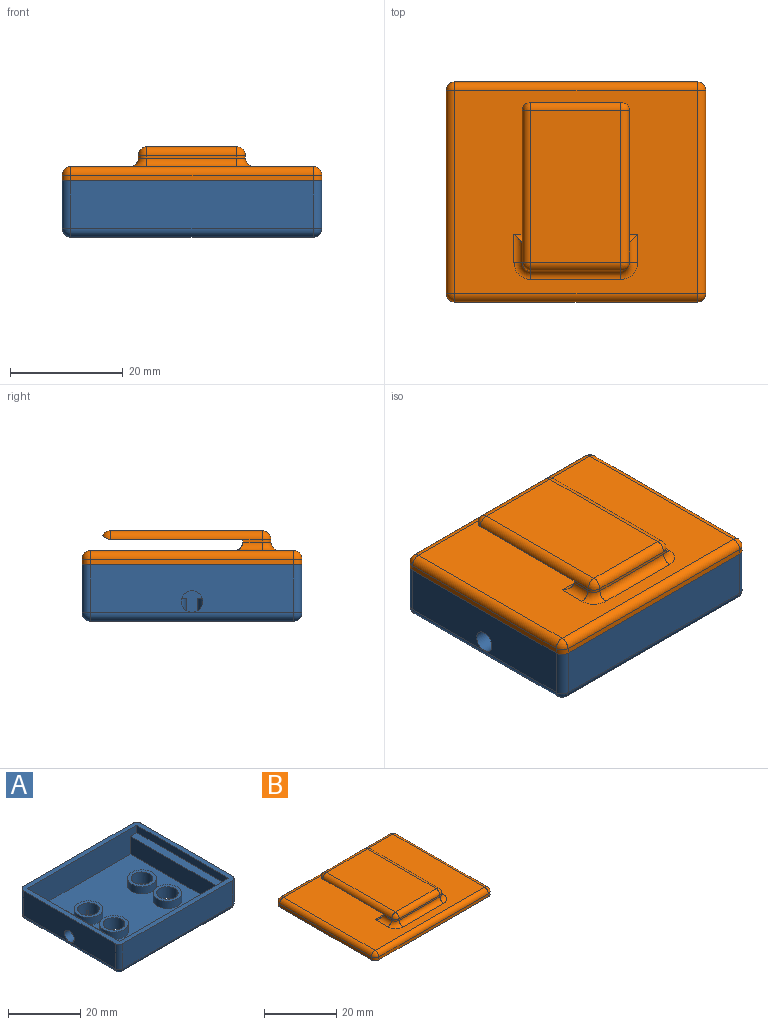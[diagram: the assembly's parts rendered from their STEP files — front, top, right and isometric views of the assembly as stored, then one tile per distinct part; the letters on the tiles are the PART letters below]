
ASSEMBLY  parts=2 mates=1
PART A: 48 faces, bbox 46x39x10 mm
  f0: plane 43x36mm, normal (0,0,-1), area 1434.9mm2, adj f18,f21,f24,f28,f32,f33,f34,f35
  f1: plane 0.57x0.49mm, normal (0,0,1), area 0mm2, adj f18,f35
  f2: plane 0.57x0.49mm, normal (0,0,1), area 0mm2, adj f21,f34
  f3: plane 43x8.5mm, normal (0,1,0), area 335.5mm2, adj f5,f7,f10,f11,f12,f13,f16,f17
  f4: plane 43x8.5mm, normal (0,-1,0), area 335.5mm2, adj f5,f7,f10,f11,f12,f13,f16,f17
  f5: plane 38x36mm, normal (0,0,1), area 1166.9mm2, adj f3,f4,f12,f17,f19,f22,f25,f29
  f6: plane 43x8.5mm, normal (0,1,0), area 365.5mm2, adj f7,f36,f41,f42
  f7: plane 46x39mm, normal (0,0,1), area 244.1mm2, adj f3,f4,f6,f8,f9,f10,f13,f15
  f8: plane 43x8.5mm, normal (0,-1,0), area 365.5mm2, adj f7,f37,f43,f44
  f9: plane 36x8.5mm, normal (1,0,0), area 306mm2, adj f7,f36,f37,f38
  f10: plane 36x2.5mm, normal (-1,0,0), area 90mm2, adj f3,f4,f7,f11
  f11: plane 36x2.5mm, normal (0,0,1), area 90mm2, adj f3,f4,f10,f12
  f12: plane 36x6mm, normal (-1,0,0), area 216mm2, adj f3,f4,f5,f11
  f13: plane 36x2.5mm, normal (1,0,0), area 90mm2, adj f3,f4,f7,f16
  f14: cylinder r=1.9mm len=4mm, axis (1,0,0), area 47.8mm2, adj f15,f17
  f15: plane 36x8.5mm, normal (-1,0,0), area 294.7mm2, adj f7,f14,f42,f43,f47
  f16: plane 36x2.5mm, normal (0,0,1), area 90mm2, adj f3,f4,f13,f17
  f17: plane 36x6mm, normal (1,0,0), area 204.7mm2, adj f3,f4,f5,f14,f16
  f18: cylinder r=3mm len=6mm, axis (0,0,-1), area 74.3mm2, adj f0,f1,f20,f35
  f19: cylinder r=4mm len=8mm, axis (0,0,-1), area 62.8mm2, adj f5,f20
  f20: plane 8x8mm, normal (0,0,1), area 22mm2, adj f18,f19
  f21: cylinder r=3mm len=6mm, axis (0,0,-1), area 74.3mm2, adj f0,f2,f23,f34
  f22: cylinder r=4mm len=8mm, axis (0,0,-1), area 62.8mm2, adj f5,f23
  f23: plane 8x8mm, normal (0,0,1), area 22mm2, adj f21,f22
  f24: cylinder r=3mm len=6mm, axis (0,0,-1), area 74.3mm2, adj f0,f26,f27,f33
  f25: cylinder r=4mm len=8mm, axis (0,0,-1), area 62.8mm2, adj f5,f26
  f26: plane 8x8mm, normal (0,0,1), area 22mm2, adj f24,f25
  f27: plane 0.57x0.49mm, normal (0,0,1), area 0mm2, adj f24,f33
  f28: cylinder r=3mm len=6mm, axis (0,0,-1), area 74.3mm2, adj f0,f30,f31,f32
  f29: cylinder r=4mm len=8mm, axis (0,0,-1), area 62.8mm2, adj f5,f30
  f30: plane 8x8mm, normal (0,0,1), area 22mm2, adj f28,f29
  f31: plane 0.57x0.49mm, normal (0,0,1), area 0mm2, adj f28,f32
  f32: plane 1.5x0.57mm, normal (-0.65,0.76,0), area 1.1mm2, adj f0,f28,f31
  f33: plane 1.5x0.57mm, normal (-0.65,-0.76,0), area 1.1mm2, adj f0,f24,f27
  f34: plane 1.5x0.57mm, normal (0.65,-0.76,0), area 1.1mm2, adj f0,f2,f21
  f35: plane 1.5x0.57mm, normal (0.65,0.76,0), area 1.1mm2, adj f0,f1,f18
  f36: cylinder r=1.5mm len=8.5mm, axis (0,0,-1), area 20mm2, adj f6,f7,f9,f39
  f37: cylinder r=1.5mm len=8.5mm, axis (0,0,1), area 20mm2, adj f7,f8,f9,f40
  f38: cylinder r=1.5mm len=36mm, axis (0,-1,0), area 84.8mm2, adj f0,f9,f39,f40
  f39: sphere r=1.5mm, area 3.5mm2, adj f36,f38,f41
  f40: sphere r=1.5mm, area 3.5mm2, adj f37,f38,f44
  f41: cylinder r=1.5mm len=43mm, axis (-1,0,0), area 101.3mm2, adj f0,f6,f39,f45
  f42: cylinder r=1.5mm len=8.5mm, axis (0,0,1), area 20mm2, adj f6,f7,f15,f45
  f43: cylinder r=1.5mm len=8.5mm, axis (0,0,-1), area 20mm2, adj f7,f8,f15,f46
  f44: cylinder r=1.5mm len=43mm, axis (-1,0,0), area 101.3mm2, adj f0,f8,f40,f46
  f45: sphere r=1.5mm, area 3.5mm2, adj f41,f42,f47
  f46: sphere r=1.5mm, area 3.5mm2, adj f43,f44,f47
  f47: cylinder r=1.5mm len=36mm, axis (0,1,0), area 84.8mm2, adj f0,f15,f45,f46
PART B: 46 faces, bbox 46x39x6 mm
  f0: cylinder r=1.5mm len=15.96mm, axis (-1,0,0), area 25.1mm2, adj f1,f2,f3,f16
  f1: sphere r=1.5mm, area 2.6mm2, adj f0,f2,f31
  f2: cylinder r=1.5mm len=18.96mm, axis (1,0,0), area 28.7mm2, adj f0,f1,f3,f20
  f3: sphere r=1.5mm, area 2.6mm2, adj f0,f2,f33
  f4: plane 18.96x0.5mm, normal (0,1,0), area 9.5mm2, adj f17,f18,f20,f22
  f5: plane 43x36mm, normal (0,0,-1), area 1548mm2, adj f11,f12,f13,f14
  f6: plane 36x1mm, normal (1,0,0), area 36mm2, adj f15,f36,f42,f45
  f7: plane 43x1mm, normal (0,1,0), area 43mm2, adj f15,f39,f43,f45
  f8: plane 36x1mm, normal (-1,0,0), area 36mm2, adj f15,f34,f38,f39
  f9: plane 43x1mm, normal (0,-1,0), area 43mm2, adj f15,f34,f36,f37
  f10: plane 43x36mm, normal (0,0,1), area 1376.2mm2, adj f21,f22,f23,f24,f25,f27,f37,f38
  f11: plane 43x1mm, normal (0,-1,0), area 43mm2, adj f5,f12,f14,f15
  f12: plane 36x1mm, normal (-1,0,0), area 36mm2, adj f5,f11,f13,f15
  f13: plane 43x1mm, normal (0,1,0), area 43mm2, adj f5,f12,f14,f15
  f14: plane 36x1mm, normal (1,0,0), area 36mm2, adj f5,f11,f13,f15
  f15: plane 46x39mm, normal (0,0,-1), area 244.1mm2, adj f6,f7,f8,f9,f11,f12,f13,f14
  f16: plane 27x15.96mm, normal (0,0,1), area 430.9mm2, adj f0,f29,f31,f33
  f17: plane 3.5x0.5mm, normal (-1,0,0), area 1.7mm2, adj f4,f25,f30,f33
  f18: plane 3.5x0.5mm, normal (1,0,0), area 1.7mm2, adj f4,f21,f26,f31
  f19: plane 15.96x0.5mm, normal (0,-1,0), area 8mm2, adj f24,f26,f29,f30
  f20: plane 23.5x18.96mm, normal (0,0,-1), area 445.5mm2, adj f2,f4,f31,f33
  f21: cylinder r=1.5mm len=5mm, axis (0,1,0), area 9.5mm2, adj f10,f18,f22,f23
  f22: cylinder r=1.5mm len=21.96mm, axis (-1,0,0), area 47.2mm2, adj f4,f10,f21,f25
  f23: torus R=3mm, axis (0,0,1), area 7.6mm2, adj f10,f21,f24,f26
  f24: cylinder r=1.5mm len=15.96mm, axis (1,0,0), area 37.6mm2, adj f10,f19,f23,f27
  f25: cylinder r=1.5mm len=5mm, axis (0,-1,0), area 9.5mm2, adj f10,f17,f22,f27
  f26: cylinder r=1.5mm len=1.5mm, axis (0,0,-1), area 1.2mm2, adj f18,f19,f23,f28
  f27: torus R=3mm, axis (0,0,1), area 7.6mm2, adj f10,f24,f25,f30
  f28: sphere r=1.5mm, area 3.5mm2, adj f26,f29,f31
  f29: cylinder r=1.5mm len=15.96mm, axis (-1,0,0), area 37.6mm2, adj f16,f19,f28,f32
  f30: cylinder r=1.5mm len=1.5mm, axis (0,0,-1), area 1.2mm2, adj f17,f19,f27,f32
  f31: cylinder r=1.5mm len=27mm, axis (0,-1,0), area 63.6mm2, adj f1,f16,f18,f20,f28
  f32: sphere r=1.5mm, area 3.5mm2, adj f29,f30,f33
  f33: cylinder r=1.5mm len=27mm, axis (0,1,0), area 63.6mm2, adj f3,f16,f17,f20,f32
  f34: cylinder r=1.5mm len=1.5mm, axis (0,0,-1), area 2.4mm2, adj f8,f9,f15,f35
  f35: sphere r=1.5mm, area 3.5mm2, adj f34,f37,f38
  f36: cylinder r=1.5mm len=1.5mm, axis (0,0,-1), area 2.4mm2, adj f6,f9,f15,f40
  f37: cylinder r=1.5mm len=43mm, axis (-1,0,0), area 101.3mm2, adj f9,f10,f35,f40
  f38: cylinder r=1.5mm len=36mm, axis (0,1,0), area 84.8mm2, adj f8,f10,f35,f41
  f39: cylinder r=1.5mm len=1.5mm, axis (0,0,1), area 2.4mm2, adj f7,f8,f15,f41
  f40: sphere r=1.5mm, area 3.5mm2, adj f36,f37,f42
  f41: sphere r=1.5mm, area 3.5mm2, adj f38,f39,f43
  f42: cylinder r=1.5mm len=36mm, axis (0,-1,0), area 84.8mm2, adj f6,f10,f40,f44
  f43: cylinder r=1.5mm len=43mm, axis (1,0,0), area 101.3mm2, adj f7,f10,f41,f44
  f44: sphere r=1.5mm, area 3.5mm2, adj f42,f43,f45
  f45: cylinder r=1.5mm len=1.5mm, axis (0,0,1), area 2.4mm2, adj f6,f7,f15,f44
PLACE A t=(-10.57,-4.65,3.88)mm
PLACE B t=(-32.23,-4.54,13.38)mm
MATE planar B.f15 <-> A.f7  axis (0,0,-1) through (-32.07,-4.65,12.38)mm
